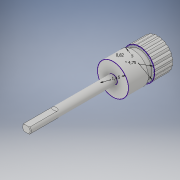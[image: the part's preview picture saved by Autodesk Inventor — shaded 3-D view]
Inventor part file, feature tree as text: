
AUTODESK INVENTOR PART (.ipt)
format: ipt  version: 2019 (Build 230136000, 136)  size: 225,280 bytes
history: native  units: mm
features: extrude x6, sketch x5, fillet x2, pattern_circular x1, hole x1
ambient origin geometry x8: Origin, YZ Plane, XZ Plane, XY Plane, X Axis, Y Axis, Z Axis, Center Point
bodies: Solid1 (feature_tree)
feature tree (15):
  sketch  "Sketch1"  dims[d0=1.4mm d1=5.0mm]
  extrude  "Extrusion1"  Depth=5.0mm
  extrude  "Extrusion2"  Depth=3.25mm TaperAngle=0.0deg
  extrude  "Extrusion3"  Depth=1.0mm TaperAngle=0.0deg
  sketch  "Sketch3"  dims[d6=4.2mm d7=1.0mm d8=0.0mm]
  extrude  "Extrusion4"  Depth=4.75mm
  extrude  "Extrusion5"  Depth=3.0mm TaperAngle=0.0deg
  pattern_circular  "Circular Pattern1"  [2 undecoded]
  hole  "Hole1"  [1 undecoded]
  fillet  "Fillet1"  Radius=0.1mm
  extrude  "Extrusion6"  Depth=1.0mm
  fillet  "Fillet2"  Radius=4.75mm
  sketch  "Sketch2"  dims[d2=14.0mm d3=0.0mm d4=3.25mm d5=0.0mm]
  sketch  "Sketch4"  dims[d9=5.0mm d10=4.75mm]
  sketch  "Sketch5"  dims[d11=0.82mm d12=3.0mm d13=0.0mm d14=3.0mm d15=0.0mm d16=200.0mm d17=360.0deg d19=2.459mm d20=6.0mm d21=3.0mm d22=2.0mm d23=90.0deg d24=5.0mm d25=20.594885mm d26=0.1mm d27=1.0mm d28=4.75mm d29=0.0mm d30=0.5mm]
note: 3 required parameter values undecoded (feature->parameter linkage not recoverable at this tier; creation-order binding heuristic only, values carry confidence <= 0.55)
